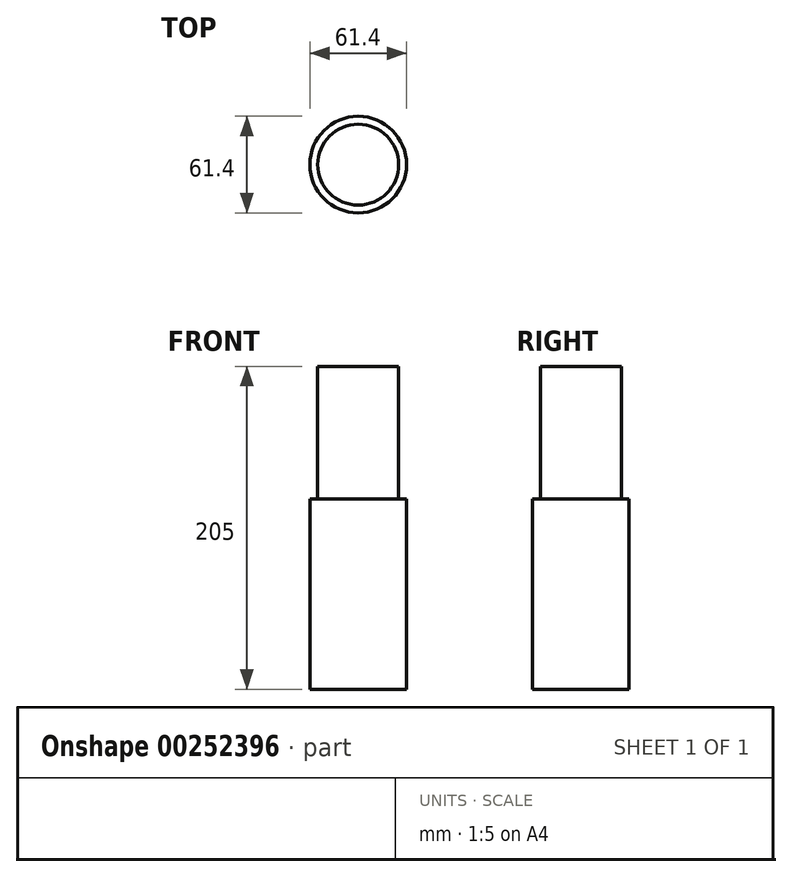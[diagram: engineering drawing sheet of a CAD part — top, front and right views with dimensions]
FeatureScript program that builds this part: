
annotation { "Feature Type Name" : "Feature", "Feature Type Description" : "" }
export const myFeature = defineFeature(function(context is Context, id is Id, definition is map)
    precondition{}
    {
        {
            var Q0;
            Q0=qCreatedBy(makeId("Front.planeOp"),FACE);
            var sketch = newSketch(context, id + "F0", { "sketchPlane" : qUnion([Q0])});
            skLineSegment(sketch, "E0.bottom", {"start": v(-30.7, -60.39) * mm, "end": v(30.7, -60.39) * mm});
            skLineSegment(sketch, "E0.top", {"start": v(-30.7, 60.39) * mm, "end": v(30.7, 60.39) * mm});
            skLineSegment(sketch, "E0.left", {"start": v(-30.7, -60.39) * mm, "end": v(-30.7, 60.39) * mm});
            skLineSegment(sketch, "E0.right", {"start": v(30.7, -60.39) * mm, "end": v(30.7, 60.39) * mm});
            skPoint(sketch, "E0.middle", {"position": v(0, 0) * mm});
            skLineSegment(sketch, "E1", {"start": v(0, 60.39) * mm, "end": v(0, -60.39) * mm});
            skSolve(sketch);
        }
        {
            var Q0;
            {var subQ0=sQuery(id+"F0.wireOp",EDGE,"E0.left");Q0=makeQuery(id+"F0.imprint","IMPRINT",FACE,{"disambiguationData":[TD([[makeQuery(id+"F0.imprint","IMPRINT",EDGE,{"derivedFrom":subQ0}),-1.0]])]});}
            var Q1;
            Q1=sQuery(id+"F0.wireOp",EDGE,"E1");
            revolve(context, id + "F1", {"entities" : qUnion([Q0]), "axis" : qUnion([Q1]), "revolveType" : RevolveType.FULL});
        }
        {
            var Q0;
            Q0=makeQuery(id+"F1.opRevolve","SWEPT_FACE",FACE,{"disambiguationData":[OSD([sQuery(id+"F0.wireOp",EDGE,"E0.top")])]});
            shell(context, id + "F2", {"entities" : qUnion([Q0]), "thickness" : 5 * mm});
        }
        {
            var Q0;
            Q0=makeQuery(id+"F2.opShell","OFFSET_FACE",FACE,{"disambiguationData":[OSD([sQuery(id+"F0.wireOp",EDGE,"E0.bottom")])]});
            extrude(context, id + "F3", {"entities" : qUnion([Q0]), "operationType" : NewBodyOperationType.ADD, "depth" : 200 * mm});
        }
    });
